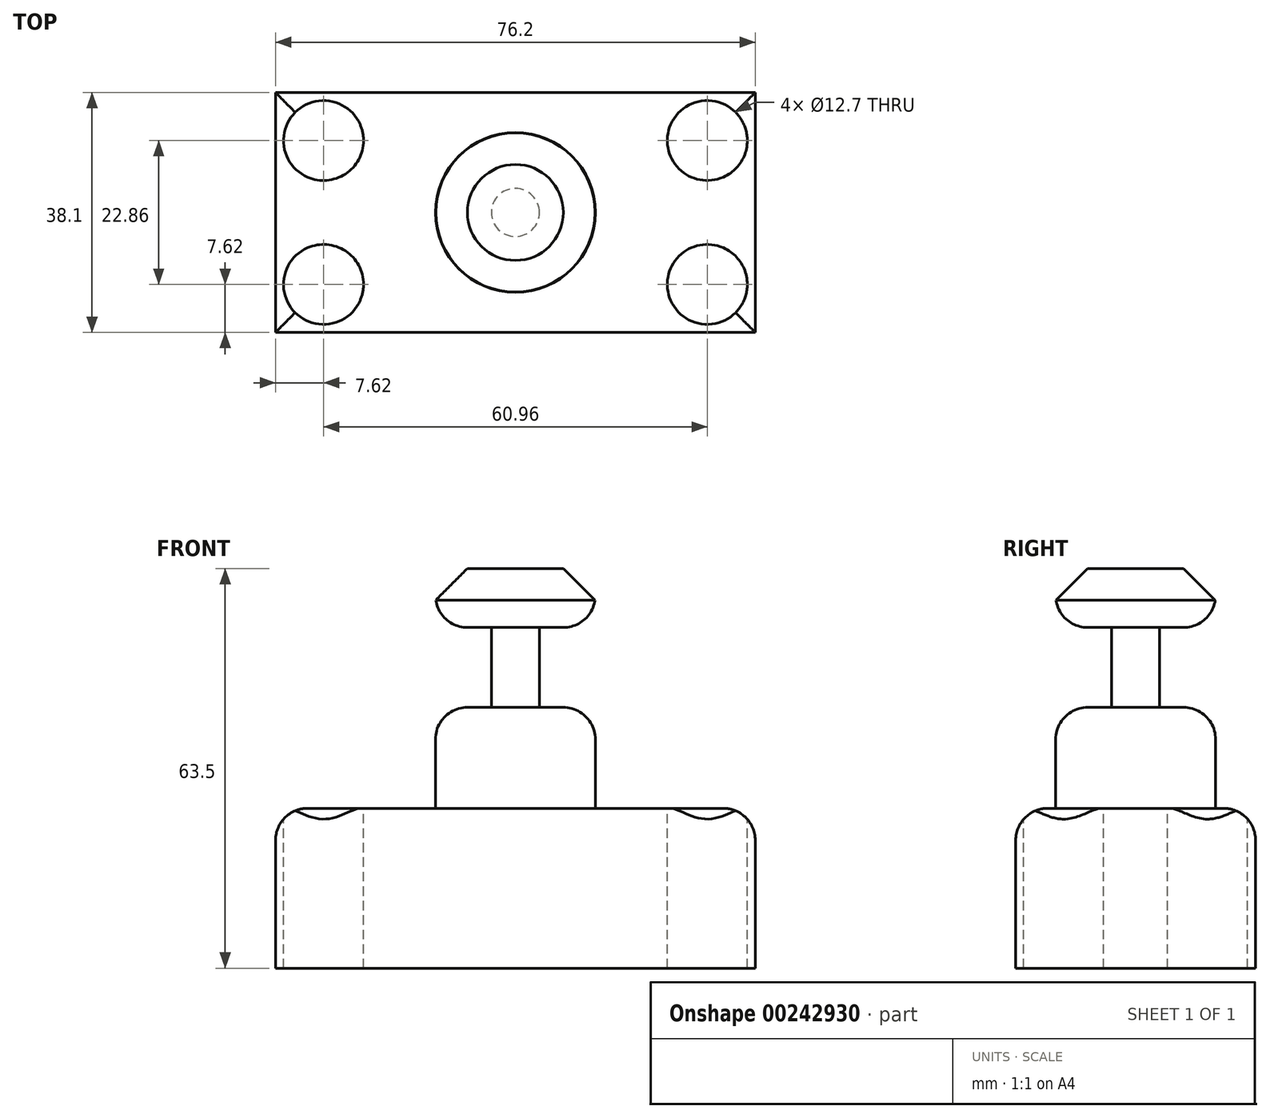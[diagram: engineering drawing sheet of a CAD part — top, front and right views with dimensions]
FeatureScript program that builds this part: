
annotation { "Feature Type Name" : "Feature", "Feature Type Description" : "" }
export const myFeature = defineFeature(function(context is Context, id is Id, definition is map)
    precondition{}
    {
        {
            var Q0;
            Q0=qCreatedBy(makeId("Top.planeOp"),FACE);
            var sketch = newSketch(context, id + "F0", { "sketchPlane" : qUnion([Q0])});
            skLineSegment(sketch, "E0.bottom", {"start": v(-38.1, 19.05) * mm, "end": v(38.1, 19.05) * mm});
            skLineSegment(sketch, "E0.top", {"start": v(-38.1, -19.05) * mm, "end": v(38.1, -19.05) * mm});
            skLineSegment(sketch, "E0.left", {"start": v(-38.1, 19.05) * mm, "end": v(-38.1, -19.05) * mm});
            skLineSegment(sketch, "E0.right", {"start": v(38.1, 19.05) * mm, "end": v(38.1, -19.05) * mm});
            skSolve(sketch);
        }
        {
            var Q0;
            Q0 = qSketchRegion(id + "F0", true);
            extrude(context, id + "F1", {"entities" : qUnion([Q0]), "depth" : 25.4 * mm});
        }
        {
            var Q0;
            Q0=makeQuery(id+"F1.opExtrude","CAP_FACE",FACE,{"disambiguationData":[OSD([sQuery(id+"F0.wireOp",EDGE,"E0.bottom"),sQuery(id+"F0.wireOp",EDGE,"E0.top"),sQuery(id+"F0.wireOp",EDGE,"E0.left"),sQuery(id+"F0.wireOp",EDGE,"E0.right")])],"isStart":false});
            var sketch = newSketch(context, id + "F2", { "sketchPlane" : qUnion([Q0])});
            skCircle(sketch, "E1", {"center": v(-30.48, 11.43) * mm, "radius": 6.35 * mm});
            skCircle(sketch, "E2", {"center": v(-30.48, -11.43) * mm, "radius": 6.35 * mm});
            skCircle(sketch, "E3", {"center": v(30.48, 11.43) * mm, "radius": 6.35 * mm});
            skCircle(sketch, "E4", {"center": v(30.48, -11.43) * mm, "radius": 6.35 * mm});
            skSolve(sketch);
        }
        {
            var Q0;
            Q0 = qSketchRegion(id + "F2", true);
            extrude(context, id + "F3", {"entities" : qUnion([Q0]), "operationType" : NewBodyOperationType.REMOVE, "oppositeDirection" : true, "depth" : 25.4 * mm});
        }
        {
            var Q0;
            Q0=makeQuery(id+"F1.opExtrude","CAP_FACE",FACE,{"disambiguationData":[OSD([sQuery(id+"F0.wireOp",EDGE,"E0.bottom"),sQuery(id+"F0.wireOp",EDGE,"E0.top"),sQuery(id+"F0.wireOp",EDGE,"E0.left"),sQuery(id+"F0.wireOp",EDGE,"E0.right")])],"isStart":false});
            var sketch = newSketch(context, id + "F4", { "sketchPlane" : qUnion([Q0])});
            skCircle(sketch, "E5", {"center": v(0, 0) * mm, "radius": 12.7 * mm});
            skSolve(sketch);
        }
        {
            var Q0;
            Q0 = qSketchRegion(id + "F4", true);
            extrude(context, id + "F5", {"entities" : qUnion([Q0]), "operationType" : NewBodyOperationType.ADD, "depth" : 38.1 * mm});
        }
        {
            var Q0;
            Q0=qCreatedBy(makeId("Front.planeOp"),FACE);
            var sketch = newSketch(context, id + "F6", { "sketchPlane" : qUnion([Q0])});
            skLineSegment(sketch, "E6.bottom", {"start": v(-16.52, 54.12) * mm, "end": v(-3.82, 54.12) * mm});
            skLineSegment(sketch, "E6.top", {"start": v(-16.52, 41.42) * mm, "end": v(-3.82, 41.42) * mm});
            skLineSegment(sketch, "E6.left", {"start": v(-16.52, 54.12) * mm, "end": v(-16.52, 41.42) * mm});
            skLineSegment(sketch, "E6.right", {"start": v(-3.82, 54.12) * mm, "end": v(-3.82, 41.42) * mm});
            skLineSegment(sketch, "E7.left", {"start": v(-16.52, 54.12) * mm, "end": v(-16.52, 54.12) * mm});
            skLineSegment(sketch, "E7.right", {"start": v(-3.82, 54.12) * mm, "end": v(-3.82, 54.12) * mm});
            skSolve(sketch);
        }
        {
            var Q0;
            Q0 = qSketchRegion(id + "F6", true);
            var Q1;
            Q1=makeQuery(id+"F5.opExtrude","CAP_EDGE",EDGE,{"disambiguationData":[OSD([sQuery(id+"F4.wireOp",EDGE,"E5")])],"isStart":false});
            revolve(context, id + "F7", {"operationType" : NewBodyOperationType.REMOVE, "entities" : qUnion([Q0]), "axis" : qUnion([Q1]), "revolveType" : RevolveType.FULL, "oppositeDirection" : true});
        }
        {
            var Q0;
            Q0=makeQuery(id+"F1.opExtrude","CAP_EDGE",EDGE,{"disambiguationData":[OSD([sQuery(id+"F0.wireOp",EDGE,"E0.top")])],"isStart":false});
            var Q1;
            Q1=makeQuery(id+"F1.opExtrude","CAP_EDGE",EDGE,{"disambiguationData":[OSD([sQuery(id+"F0.wireOp",EDGE,"E0.left")])],"isStart":false});
            var Q2;
            Q2=makeQuery(id+"F1.opExtrude","CAP_EDGE",EDGE,{"disambiguationData":[OSD([sQuery(id+"F0.wireOp",EDGE,"E0.bottom")])],"isStart":false});
            var Q3;
            Q3=makeQuery(id+"F1.opExtrude","CAP_EDGE",EDGE,{"disambiguationData":[OSD([sQuery(id+"F0.wireOp",EDGE,"E0.right")])],"isStart":false});
            var Q4;
            Q4=makeQuery(id+"F7.boolean.opBoolean","INTERSECT",EDGE,{"derivedFrom":[makeQuery(id+"F5.opExtrude","SWEPT_FACE",FACE,{"disambiguationData":[OSD([sQuery(id+"F4.wireOp",EDGE,"E5")])]}),makeQuery(id+"F7.opRevolve","SWEPT_FACE",FACE,{"disambiguationData":[OSD([sQuery(id+"F6.wireOp",EDGE,"E6.top")])]})]});
            var Q5;
            Q5=makeQuery(id+"F7.boolean.opBoolean","INTERSECT",EDGE,{"derivedFrom":[makeQuery(id+"F5.opExtrude","SWEPT_FACE",FACE,{"disambiguationData":[OSD([sQuery(id+"F4.wireOp",EDGE,"E5")])]}),makeQuery(id+"F7.opRevolve","SWEPT_FACE",FACE,{"disambiguationData":[OSD([sQuery(id+"F6.wireOp",EDGE,"E6.bottom")])]})]});
            fillet(context, id + "F8", {"entities" : qUnion([Q0, Q1, Q2, Q3, Q4, Q5]), "radius" : 5.08 * mm, "tangentPropagation" : true, "allowEdgeOverflow" : false});
        }
        {
            var Q0;
            Q0=makeQuery(id+"F5.opExtrude","CAP_EDGE",EDGE,{"disambiguationData":[OSD([sQuery(id+"F4.wireOp",EDGE,"E5")])],"isStart":false});
            chamfer(context, id + "F9", {"entities" : qUnion([Q0]), "width" : 5.08 * mm, "tangentPropagation" : true});
        }
    });
